# Revit family: Sense Plus allas
name_source: partatom
category: Casework
revit_build: Autodesk Revit 2016 (Build: 20161004_0715(x64)
units: mm (PartAtom-declared; Revit-internal decimal feet)

## family parameters
Always vertical = Yes
Cut with Voids When Loaded = No
OmniClass Number = 23.40.35.00
OmniClass Title = Casework
Room Calculation Point = No
Shared = No
Work Plane-Based = No

## types (6) — shared parameters
Depth = 600 mm
Height = 800 mm  [stored 2.62467 ft]
Manufacturer = Väinö Korpinen Oy
Model = Sense Plus allas
URL = www.korpinen.com
Width = 1400 mm  [stored 4.59318 ft]

## per-type parameters (varying)
| type | Accent color | Basin left | Basin right |
| 62081WAM | Cast Marble - White | No | Yes |
| 62081RAM | Red | No | Yes |
| 62081GAM | Grey | No | Yes |
| 62082GAM | Grey | Yes | No |
| 62082RAM | Red | Yes | No |
| 62082WAM | Cast Marble - White | Yes | No |

note: [stored X ft] marks values corroborated as IEEE doubles in the binary element streams (Revit-internal decimal feet)

## geometry (parser evidence)
native form markers: Blend x6, Sweep x7
no freeform markers — native parametric forms only
